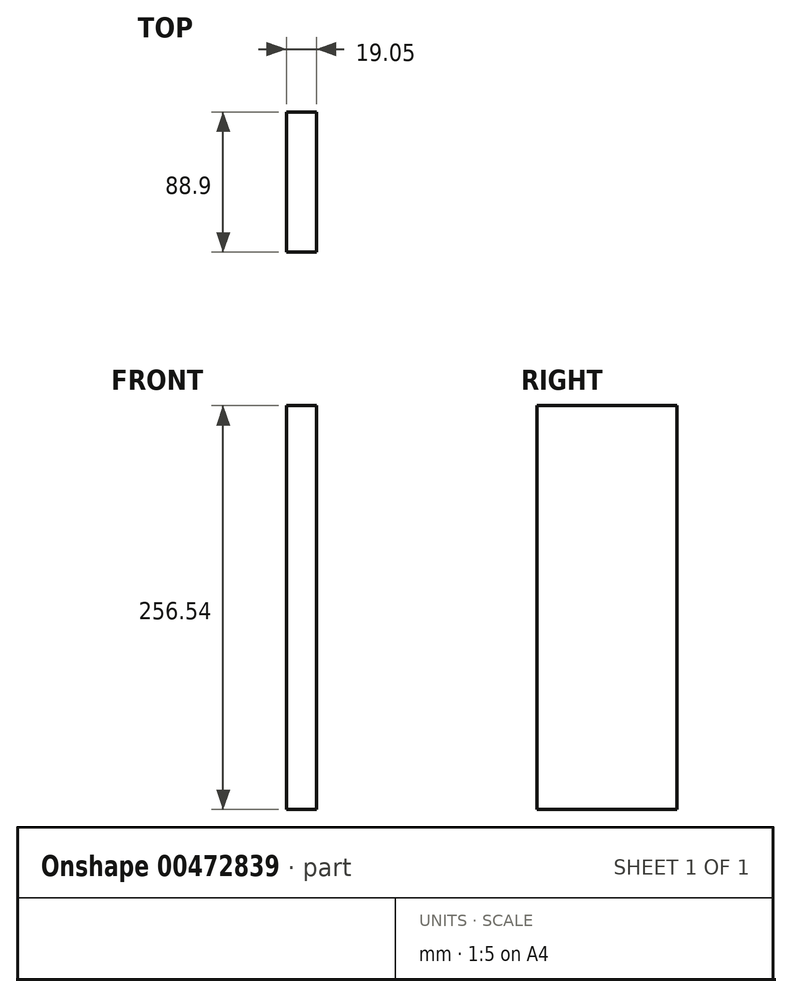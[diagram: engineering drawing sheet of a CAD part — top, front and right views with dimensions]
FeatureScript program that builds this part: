
annotation { "Feature Type Name" : "Feature", "Feature Type Description" : "" }
export const myFeature = defineFeature(function(context is Context, id is Id, definition is map)
    precondition{}
    {
        {
            var Q0;
            Q0=qCreatedBy(makeId("Right.planeOp"),FACE);
            var sketch = newSketch(context, id + "F0", { "sketchPlane" : qUnion([Q0])});
            skLineSegment(sketch, "E0.bottom", {"start": v(44.45, 128.27) * mm, "end": v(-44.45, 128.27) * mm});
            skLineSegment(sketch, "E0.top", {"start": v(44.45, -128.27) * mm, "end": v(-44.45, -128.27) * mm});
            skLineSegment(sketch, "E0.left", {"start": v(44.45, 128.27) * mm, "end": v(44.45, -128.27) * mm});
            skLineSegment(sketch, "E0.right", {"start": v(-44.45, 128.27) * mm, "end": v(-44.45, -128.27) * mm});
            skPoint(sketch, "E0.middle", {"position": v(0, 0) * mm});
            skSolve(sketch);
        }
        {
            var Q0;
            Q0=makeQuery(id+"F0.imprint","IMPRINT",FACE,{"disambiguationData":[TD([[makeQuery(id+"F0.imprint","IMPRINT",EDGE,{"derivedFrom":sQuery(id+"F0.wireOp",EDGE,"E0.bottom")}),1.0]])]});
            extrude(context, id + "F1", {"entities" : qUnion([Q0]), "depth" : 19.05 * mm});
        }
    });
